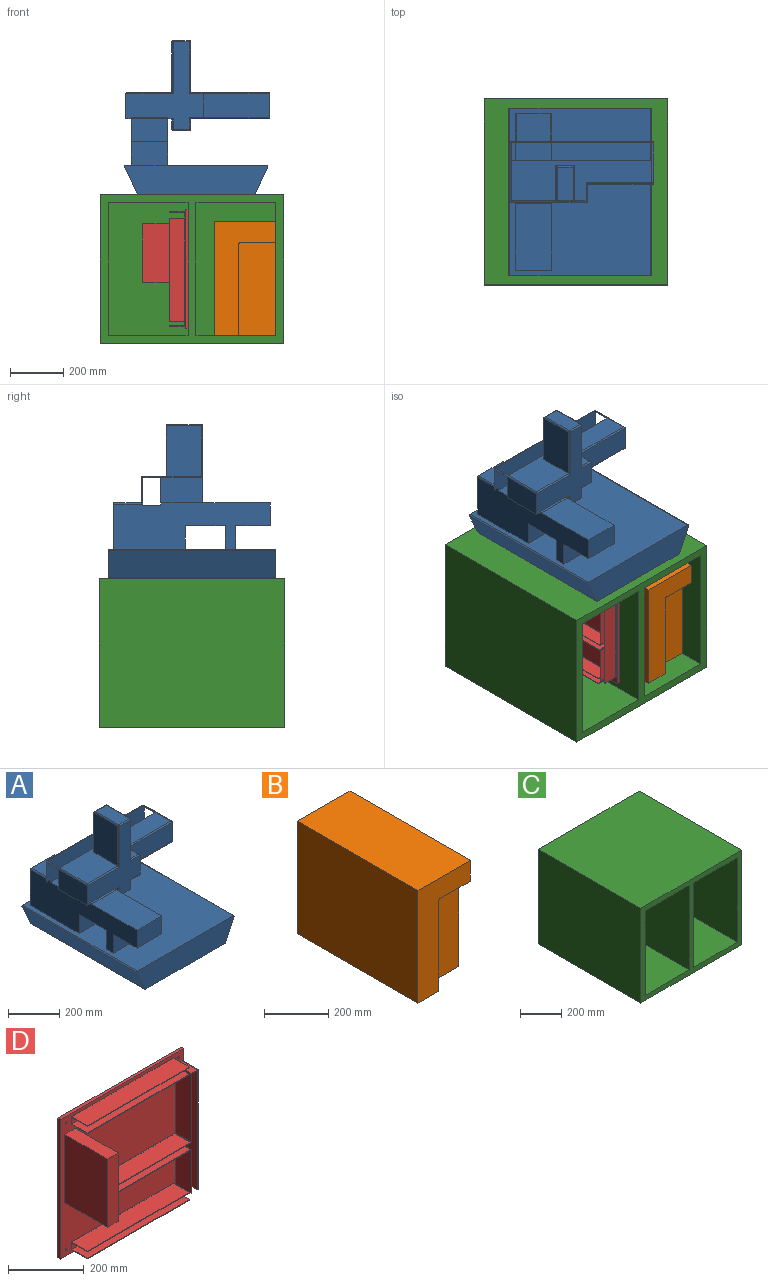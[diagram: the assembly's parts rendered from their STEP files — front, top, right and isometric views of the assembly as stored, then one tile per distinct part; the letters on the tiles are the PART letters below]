
ASSEMBLY  parts=4 mates=4
PART A: 86 faces, bbox 545x630x580 mm
  f0: plane 157.49x20mm, normal (0,0,-1), area 3142.4mm2, adj f1,f3,f26,f27,f79,f84
  f1: plane 100x68mm, normal (1,0,0), area 386.4mm2, adj f0,f43,f79,f81,f84,f85
  f2: plane 530x152mm, normal (0,0,1), area 54313.4mm2, adj f30,f31,f32,f43,f44,f52,f54,f55
  f3: plane 590x180mm, normal (-1,0,0), area 76782.9mm2, adj f0,f5,f8,f18,f19,f20,f21,f22
  f4: plane 590x180mm, normal (1,0,0), area 76788.2mm2, adj f6,f8,f18,f19,f20,f21,f22,f23
  f5: plane 20x5mm, normal (0,0,-1), area 94.6mm2, adj f3,f29,f69,f81
  f6: plane 383x157.87mm, normal (0,0,-1), area 31730.7mm2, adj f4,f27,f28,f34,f35,f36,f40,f41
  f7: plane 127x104.9mm, normal (0,0,1), area 13322.6mm2, adj f19,f29,f62,f63
  f8: plane 630x530mm, normal (0,0,1), area 291430mm2, adj f3,f4,f9,f10,f12,f13,f19,f21
  f9: plane 540x110mm, normal (0,-1,0), area 54240.7mm2, adj f8,f11,f12,f13,f14,f15,f16,f17
  f10: plane 540x110mm, normal (0,1,0), area 54240.7mm2, adj f8,f11,f12,f13,f14,f15,f16,f17
  f11: plane 630x435.63mm, normal (0,0,-1), area 274446.9mm2, adj f9,f10,f16,f17
  f12: cylinder r=5mm len=630mm, axis (0,1,0), area 4948mm2, adj f8,f9,f10,f15
  f13: cylinder r=5mm len=630mm, axis (0,-1,0), area 4948mm2, adj f8,f9,f10,f14
  f14: plane 630x102.11mm, normal (0.91,0,-0.42), area 70981.7mm2, adj f9,f10,f13,f16
  f15: plane 630x102.12mm, normal (-0.91,0,-0.42), area 71003.5mm2, adj f9,f10,f12,f17
  f16: cylinder r=5mm len=630mm, axis (0,-1,0), area 3573.6mm2, adj f9,f10,f11,f14
  f17: cylinder r=5mm len=630mm, axis (0,1,0), area 3571.7mm2, adj f9,f10,f11,f15
  f18: plane 137x85mm, normal (0,-1,0), area 11645mm2, adj f3,f4,f20,f22
  f19: plane 175x137mm, normal (0,1,0), area 23964.3mm2, adj f3,f4,f7,f8,f62,f63
  f20: plane 250.1x137mm, normal (0,0,1), area 34263.4mm2, adj f3,f4,f18,f61
  f21: plane 137x90mm, normal (0,-1,0), area 12330mm2, adj f3,f4,f8,f22
  f22: plane 137x130mm, normal (0,0,-1), area 17810mm2, adj f3,f4,f18,f21
  f23: plane 137x90mm, normal (0,-1,0), area 12330mm2, adj f3,f4,f8,f25
  f24: plane 137x90mm, normal (0,1,0), area 12330mm2, adj f3,f4,f8,f25
  f25: plane 150x137mm, normal (0,0,-1), area 20550mm2, adj f3,f4,f23,f24
  f26: plane 157.49x95mm, normal (-1,0,0), area 14961.4mm2, adj f0,f27,f43,f84
  f27: plane 329x291.73mm, normal (0,-1,0), area 40803.9mm2, adj f0,f3,f4,f6,f26,f39,f40,f44
  f28: plane 95x89.37mm, normal (1,0,0), area 8484.4mm2, adj f6,f38,f42,f52,f83
  f29: plane 530x100mm, normal (0,1,0), area 48470.7mm2, adj f3,f4,f5,f7,f62,f63,f64,f65
  f30: plane 190x132mm, normal (1,0,0), area 25080mm2, adj f2,f31,f50,f53
  f31: plane 190x70mm, normal (0,1,0), area 13300mm2, adj f2,f30,f32,f48
  f32: plane 190x132mm, normal (-1,0,0), area 25080mm2, adj f2,f31,f45,f46
  f33: plane 127x60mm, normal (0,0,1), area 7620mm2, adj f46,f48,f49,f50
  f34: plane 127x39mm, normal (1,0,0), area 4953mm2, adj f6,f58,f72,f74
  f35: plane 60x39mm, normal (0,1,0), area 2340mm2, adj f6,f60,f70,f72
  f36: plane 127x39mm, normal (-1,0,0), area 4953mm2, adj f6,f59,f70,f76
  f37: plane 127x60mm, normal (0,0,-1), area 7620mm2, adj f57,f58,f59,f60
  f38: plane 248.27x90mm, normal (0,-1,0), area 22344.4mm2, adj f28,f39,f42,f54
  f39: plane 90x68.5mm, normal (1,0,0), area 6165mm2, adj f27,f38,f41,f56
  f40: cylinder r=5mm len=53.06mm, axis (1,0,0), area 377.5mm2, adj f6,f27,f41,f74
  f41: cylinder r=5mm len=73.5mm, axis (0,-1,0), area 538mm2, adj f6,f39,f40,f42
  f42: cylinder r=5mm len=253.27mm, axis (-1,0,0), area 1964.2mm2, adj f6,f28,f38,f41
  f43: cylinder r=5mm len=225mm, axis (0,1,0), area 1752.9mm2, adj f1,f2,f26,f44,f68,f85
  f44: cylinder r=5mm len=178.67mm, axis (-1,0,0), area 1364mm2, adj f2,f27,f43,f45
  f45: cylinder r=5mm len=195mm, axis (0,0,1), area 1506.5mm2, adj f27,f32,f44,f47
  f46: cylinder r=5mm len=132mm, axis (0,1,0), area 1022.5mm2, adj f32,f33,f47,f48
  f47: sphere r=5mm, area 39.3mm2, adj f45,f46,f49
  f48: cylinder r=5mm len=70mm, axis (1,0,0), area 521.2mm2, adj f31,f33,f46,f50
  f49: cylinder r=5mm len=60mm, axis (-1,0,0), area 471.2mm2, adj f27,f33,f47,f51
  f50: cylinder r=5mm len=132mm, axis (0,-1,0), area 1022.5mm2, adj f30,f33,f48,f51
  f51: sphere r=5mm, area 39.3mm2, adj f49,f50,f53
  f52: cylinder r=5mm len=156.5mm, axis (0,-1,0), area 1214.9mm2, adj f2,f28,f54,f66,f80,f82
  f53: cylinder r=5mm len=195mm, axis (0,0,-1), area 1506.5mm2, adj f27,f30,f51,f55
  f54: cylinder r=5mm len=253.27mm, axis (1,0,0), area 1949.9mm2, adj f2,f38,f52,f56
  f55: cylinder r=5mm len=53.06mm, axis (-1,0,0), area 377.5mm2, adj f2,f27,f53,f56
  f56: cylinder r=5mm len=73.5mm, axis (0,1,0), area 538mm2, adj f2,f39,f54,f55
  f57: cylinder r=5mm len=60mm, axis (1,0,0), area 471.2mm2, adj f27,f37,f75,f77
  f58: cylinder r=5mm len=127mm, axis (0,-1,0), area 997.5mm2, adj f34,f37,f73,f75
  f59: cylinder r=5mm len=127mm, axis (0,1,0), area 997.5mm2, adj f36,f37,f71,f77
  f60: cylinder r=5mm len=60mm, axis (1,0,0), area 471.2mm2, adj f35,f37,f71,f73
  f61: cylinder r=5mm len=137mm, axis (1,0,0), area 1076mm2, adj f3,f4,f20,f27
  f62: cylinder r=5mm len=104.9mm, axis (0,-1,0), area 823.9mm2, adj f4,f7,f19,f29
  f63: cylinder r=5mm len=104.9mm, axis (0,1,0), area 823.9mm2, adj f3,f7,f19,f29
  f64: cylinder r=5mm len=383mm, axis (-1,0,0), area 2993.8mm2, adj f4,f29,f65,f81
  f65: cylinder r=5mm len=95mm, axis (0,0,-1), area 731.9mm2, adj f29,f64,f66,f81
  f66: sphere r=5mm, area 39.3mm2, adj f52,f65,f67
  f67: cylinder r=5mm len=530mm, axis (1,0,0), area 4162.6mm2, adj f29,f66,f68,f81
  f68: sphere r=5mm, area 39.3mm2, adj f43,f67,f69
  f69: cylinder r=5mm len=95mm, axis (0,0,1), area 746.1mm2, adj f5,f29,f68,f81
  f70: cylinder r=5mm len=39mm, axis (0,0,-1), area 306.3mm2, adj f6,f35,f36,f71
  f71: sphere r=5mm, area 39.3mm2, adj f59,f60,f70
  f72: cylinder r=5mm len=39mm, axis (0,0,1), area 306.3mm2, adj f6,f34,f35,f73
  f73: sphere r=5mm, area 39.3mm2, adj f58,f60,f72
  f74: cylinder r=5mm len=44mm, axis (0,0,-1), area 320.6mm2, adj f27,f34,f40,f75
  f75: sphere r=5mm, area 39.3mm2, adj f57,f58,f74
  f76: cylinder r=5mm len=39mm, axis (0,0,1), area 306.3mm2, adj f6,f27,f36,f77
  f77: sphere r=5mm, area 39.3mm2, adj f57,f59,f76
  f78: plane 137x68mm, normal (0,0,1), area 9316mm2, adj f3,f4,f79,f81
  f79: plane 530x111mm, normal (0,1,0), area 54507mm2, adj f0,f1,f2,f3,f4,f6,f78,f80
  f80: plane 100x68mm, normal (-1,0,0), area 422.3mm2, adj f6,f52,f79,f81,f82,f83
  f81: plane 540x111mm, normal (0,-1,0), area 55457mm2, adj f1,f3,f4,f5,f64,f65,f67,f69
  f82: plane 67.13x5mm, normal (0,0,-1), area 335.7mm2, adj f52,f80,f81,f83
  f83: plane 95x5mm, normal (0,1,0), area 475mm2, adj f6,f28,f80,f82
  f84: plane 95x5mm, normal (0,1,0), area 475mm2, adj f0,f1,f26,f85
  f85: plane 67.51x5mm, normal (0,0,-1), area 337.6mm2, adj f1,f43,f81,f84
PART B: 10 faces, bbox 230x530x430 mm
  f0: plane 430x230mm, normal (0,-1,0), area 49921.5mm2, adj f1,f2,f3,f4,f6,f7,f9
  f1: plane 530x230mm, normal (0,0,-1), area 114900mm2, adj f0,f2,f4,f5,f6,f8
  f2: plane 530x430mm, normal (1,0,0), area 210400mm2, adj f0,f1,f3,f5,f7,f8
  f3: plane 530x230mm, normal (0,0,1), area 121900mm2, adj f0,f2,f4,f5
  f4: plane 530x430mm, normal (-1,0,0), area 227900mm2, adj f0,f1,f3,f5
  f5: plane 430x230mm, normal (0,1,0), area 98900mm2, adj f1,f2,f3,f4
  f6: plane 340x50mm, normal (1,0,0), area 17000mm2, adj f0,f1,f8,f9
  f7: plane 130x50mm, normal (0,0,-1), area 6500mm2, adj f0,f2,f8,f9
  f8: plane 350x140mm, normal (0,-1,0), area 48978.5mm2, adj f1,f2,f6,f7,f9
  f9: cylinder r=10mm len=50mm, axis (0,-1,0), area 785.4mm2, adj f0,f6,f7,f8
PART C: 16 faces, bbox 690x700x560 mm
  f0: plane 700x560mm, normal (1,0,0), area 392000mm2, adj f1,f11,f12,f13
  f1: plane 700x690mm, normal (0,0,1), area 483000mm2, adj f0,f2,f12,f13
  f2: plane 700x560mm, normal (-1,0,0), area 392000mm2, adj f1,f11,f12,f13
  f3: plane 670x300mm, normal (0,0,1), area 201000mm2, adj f4,f9,f12,f14
  f4: plane 670x500mm, normal (1,0,0), area 335000mm2, adj f3,f5,f12,f14
  f5: plane 670x300mm, normal (0,0,-1), area 201000mm2, adj f4,f9,f12,f14
  f6: plane 670x300mm, normal (0,0,1), area 201000mm2, adj f7,f10,f12,f15
  f7: plane 670x500mm, normal (1,0,0), area 335000mm2, adj f6,f8,f12,f15
  f8: plane 670x300mm, normal (0,0,-1), area 201000mm2, adj f7,f10,f12,f15
  f9: plane 670x500mm, normal (-1,0,0), area 335000mm2, adj f3,f5,f12,f14
  f10: plane 670x500mm, normal (-1,0,0), area 335000mm2, adj f6,f8,f12,f15
  f11: plane 700x690mm, normal (0,0,-1), area 483000mm2, adj f0,f2,f12,f13
  f12: plane 690x560mm, normal (0,-1,0), area 86400mm2, adj f0,f1,f2,f3,f4,f5,f6,f7
  f13: plane 690x560mm, normal (0,1,0), area 386400mm2, adj f0,f1,f2,f11
  f14: plane 500x300mm, normal (0,-1,0), area 150000mm2, adj f3,f4,f5,f9
  f15: plane 500x300mm, normal (0,-1,0), area 150000mm2, adj f6,f7,f8,f10
PART D: 55 faces, bbox 460x170x450 mm
  f0: plane 365x2mm, normal (0,-1,0), area 730mm2, adj f1,f2,f50,f52
  f1: plane 60x25mm, normal (1,0,0), area 282mm2, adj f0,f6,f49,f50,f51,f52,f53,f54
  f2: plane 60x25mm, normal (-1,0,0), area 282mm2, adj f0,f6,f49,f50,f51,f52,f53,f54
  f3: plane 140.78x2mm, normal (0,-1,0), area 281.6mm2, adj f4,f39,f40,f47
  f4: plane 140.78x58mm, normal (1,0,0), area 8165.3mm2, adj f3,f40,f45,f47
  f5: plane 387.5x25mm, normal (0,-1,0), area 1241.5mm2, adj f39,f40,f41,f42,f43,f44,f46,f48
  f6: plane 460x450mm, normal (0,-1,0), area 160309mm2, adj f1,f2,f8,f10,f11,f13,f14,f15
  f7: plane 380x2mm, normal (0,-1,0), area 760mm2, adj f8,f29,f31,f38
  f8: plane 60x25mm, normal (1,0,0), area 282mm2, adj f6,f7,f30,f31,f32,f36,f37,f38
  f9: plane 380x2mm, normal (0,-1,0), area 760mm2, adj f10,f11,f27,f33
  f10: plane 60x25mm, normal (-1,0,0), area 282mm2, adj f6,f9,f26,f27,f28,f33,f34,f35
  f11: plane 60x25mm, normal (1,0,0), area 282mm2, adj f6,f9,f26,f27,f28,f33,f34,f35
  f12: plane 460x450mm, normal (0,1,0), area 206921.5mm2, adj f13,f14,f15,f16,f17,f18,f19,f20
  f13: plane 460x10mm, normal (0,0,-1), area 4600mm2, adj f6,f12,f14,f16
  f14: plane 450x10mm, normal (1,0,0), area 4500mm2, adj f6,f12,f13,f15
  f15: plane 460x10mm, normal (0,0,1), area 4600mm2, adj f6,f12,f14,f16
  f16: plane 450x10mm, normal (-1,0,0), area 4500mm2, adj f6,f12,f13,f15
  f17: cylinder r=2.5mm len=10mm, axis (0,-1,0), area 157.1mm2, adj f6,f12
  f18: cylinder r=2.5mm len=10mm, axis (0,-1,0), area 157.1mm2, adj f6,f12
  f19: cylinder r=2.5mm len=10mm, axis (0,-1,0), area 157.1mm2, adj f6,f12
  f20: cylinder r=2.5mm len=10mm, axis (0,-1,0), area 157.1mm2, adj f6,f12
  f21: plane 220x160mm, normal (-1,0,0), area 35200mm2, adj f6,f22,f24,f25
  f22: plane 160x40mm, normal (0,0,-1), area 6400mm2, adj f6,f21,f23,f25
  f23: plane 220x160mm, normal (1,0,0), area 35200mm2, adj f6,f22,f24,f25
  f24: plane 160x40mm, normal (0,0,1), area 6400mm2, adj f6,f21,f23,f25
  f25: plane 220x40mm, normal (0,-1,0), area 8800mm2, adj f21,f22,f23,f24
  f26: plane 380x60mm, normal (0,0,-1), area 22800mm2, adj f6,f10,f11,f28
  f27: plane 380x60mm, normal (0,0,1), area 22800mm2, adj f6,f9,f10,f11
  f28: plane 380x2mm, normal (0,-1,0), area 760mm2, adj f10,f11,f26,f34
  f29: plane 60x25mm, normal (-1,0,0), area 282mm2, adj f6,f7,f30,f31,f32,f36,f37,f38
  f30: plane 380x60mm, normal (0,0,-1), area 22800mm2, adj f6,f8,f29,f32
  f31: plane 380x60mm, normal (0,0,1), area 22800mm2, adj f6,f7,f8,f29
  f32: plane 380x2mm, normal (0,-1,0), area 760mm2, adj f8,f29,f30,f36
  f33: plane 380x58mm, normal (0,0,-1), area 22040mm2, adj f9,f10,f11,f35
  f34: plane 380x58mm, normal (0,0,1), area 22040mm2, adj f10,f11,f28,f35
  f35: plane 380x21mm, normal (0,-1,0), area 7980mm2, adj f10,f11,f33,f34
  f36: plane 380x58mm, normal (0,0,1), area 22040mm2, adj f8,f29,f32,f37
  f37: plane 380x21mm, normal (0,-1,0), area 7980mm2, adj f8,f29,f36,f38
  f38: plane 380x58mm, normal (0,0,-1), area 22040mm2, adj f7,f8,f29,f37
  f39: plane 387.5x60mm, normal (-1,0,0), area 21800mm2, adj f3,f5,f6,f40,f42,f45,f47,f48
  f40: plane 60x25mm, normal (0,0,-1), area 282mm2, adj f3,f4,f5,f6,f39,f41,f43,f45
  f41: plane 387.5x60mm, normal (1,0,0), area 23250mm2, adj f5,f6,f40,f42
  f42: plane 60x25mm, normal (0,0,1), area 1500mm2, adj f5,f6,f39,f41
  f43: plane 386.4x58mm, normal (-1,0,0), area 22411.2mm2, adj f5,f40,f45,f46
  f44: plane 220.62x58mm, normal (1,0,0), area 12795.9mm2, adj f5,f45,f46,f48
  f45: plane 386.4x23mm, normal (0,-1,0), area 8164.4mm2, adj f4,f39,f40,f43,f44,f46,f47,f48
  f46: plane 58x21mm, normal (0,0,-1), area 1218mm2, adj f5,f43,f44,f45
  f47: plane 58x2mm, normal (0,0,1), area 116mm2, adj f3,f4,f39,f45
  f48: plane 58x2mm, normal (0,0,-1), area 116mm2, adj f5,f39,f44,f45
  f49: plane 365x60mm, normal (0,0,-1), area 21900mm2, adj f1,f2,f6,f51
  f50: plane 365x60mm, normal (0,0,1), area 21900mm2, adj f0,f1,f2,f6
  f51: plane 365x2mm, normal (0,-1,0), area 730mm2, adj f1,f2,f49,f53
  f52: plane 365x58mm, normal (0,0,-1), area 21170mm2, adj f0,f1,f2,f54
  f53: plane 365x58mm, normal (0,0,1), area 21170mm2, adj f1,f2,f51,f54
  f54: plane 365x21mm, normal (0,-1,0), area 7665mm2, adj f1,f2,f52,f53
PLACE A t=(-174.15,-102.86,237.74)mm
PLACE B t=(9.89,-402.82,-77.26)mm
PLACE C t=(-190.11,247.14,-42.26)mm fixed
PLACE D rot(axis=(0,0,-1),90deg) t=(-205.11,-117.86,-42.26)mm
MATE planar B.f2 <-> C.f10  axis (1,0,0) through (124.89,-117.86,-73.93)mm
MATE planar D.f12 <-> C.f9  axis (1,0,0) through (-205.11,-117.86,-42.26)mm
MATE planar B.f1 <-> C.f6  axis (0,0,-1) through (7.15,-123.2,-292.26)mm
MATE planar A.f11 <-> C.f1  axis (0,0,-1) through (-174.11,-102.86,237.74)mm
